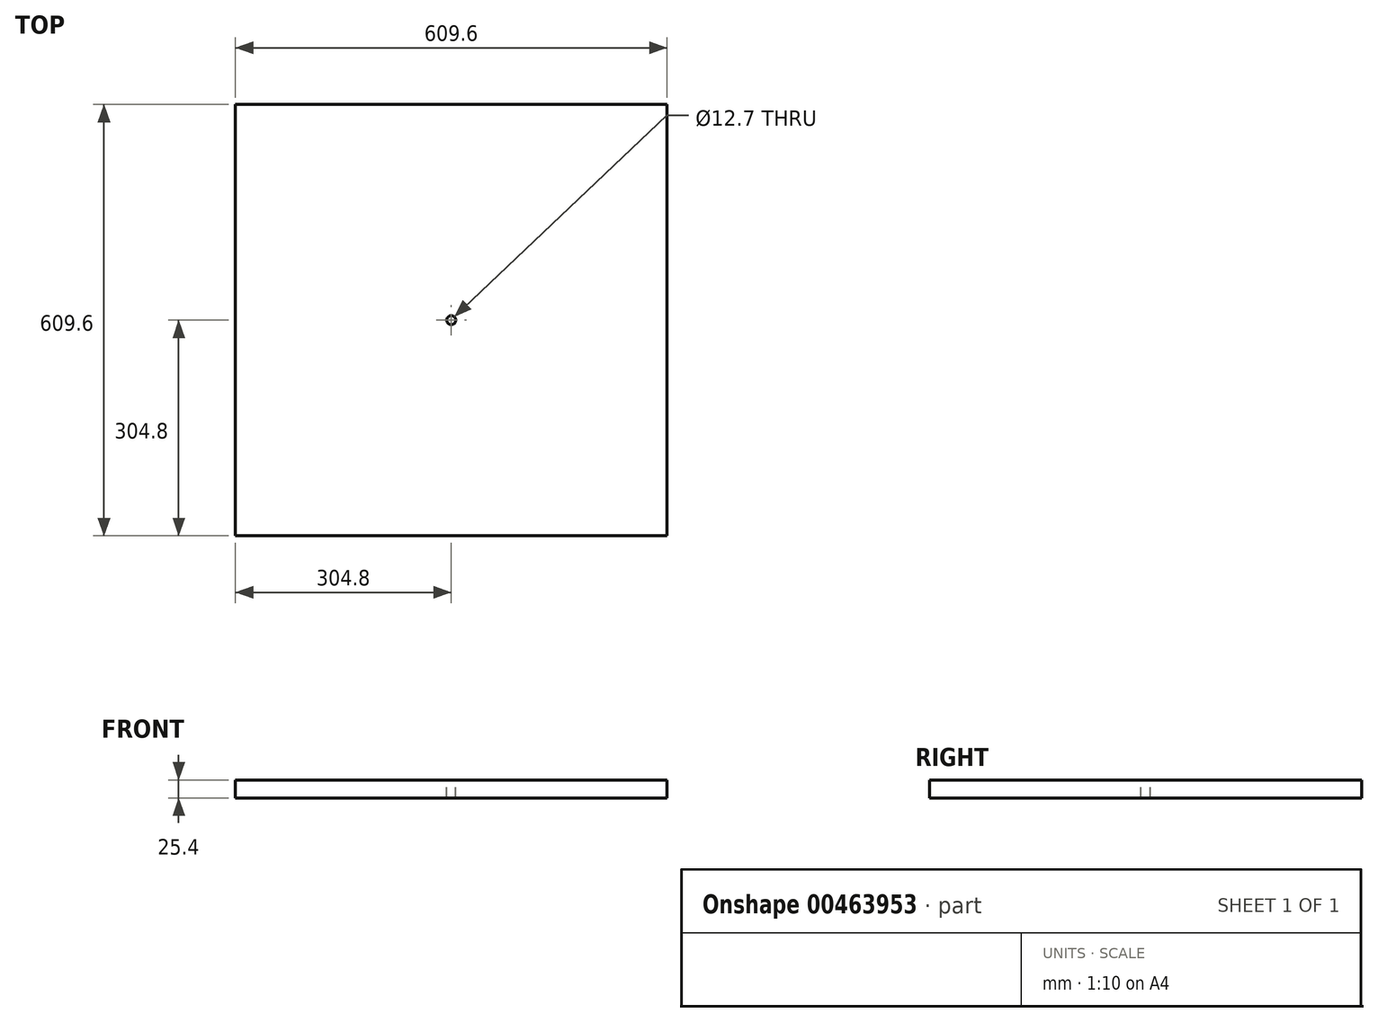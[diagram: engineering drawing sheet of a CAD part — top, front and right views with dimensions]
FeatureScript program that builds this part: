
annotation { "Feature Type Name" : "Feature", "Feature Type Description" : "" }
export const myFeature = defineFeature(function(context is Context, id is Id, definition is map)
    precondition{}
    {
        {
            var Q0;
            Q0=qCreatedBy(makeId("Top.planeOp"),FACE);
            var sketch = newSketch(context, id + "F0", { "sketchPlane" : qUnion([Q0])});
            skLineSegment(sketch, "E0.bottom", {"start": v(304.8, 304.8) * mm, "end": v(-304.8, 304.8) * mm});
            skLineSegment(sketch, "E0.top", {"start": v(304.8, -304.8) * mm, "end": v(-304.8, -304.8) * mm});
            skLineSegment(sketch, "E0.left", {"start": v(304.8, 304.8) * mm, "end": v(304.8, -304.8) * mm});
            skLineSegment(sketch, "E0.right", {"start": v(-304.8, 304.8) * mm, "end": v(-304.8, -304.8) * mm});
            skPoint(sketch, "E0.middle", {"position": v(0, 0) * mm});
            skSolve(sketch);
        }
        {
            var Q0;
            Q0 = qSketchRegion(id + "F0", true);
            extrude(context, id + "F1", {"entities" : qUnion([Q0]), "depth" : 25.4 * mm, "offsetDistance" : 25.4 * mm});
        }
        {
            var Q0;
            Q0=makeQuery(id+"F1.opExtrude","CAP_FACE",FACE,{"disambiguationData":[OSD([sQuery(id+"F0.wireOp",EDGE,"E0.bottom"),sQuery(id+"F0.wireOp",EDGE,"E0.top"),sQuery(id+"F0.wireOp",EDGE,"E0.left"),sQuery(id+"F0.wireOp",EDGE,"E0.right")])],"isStart":false});
            var sketch = newSketch(context, id + "F2", { "sketchPlane" : qUnion([Q0])});
            skCircle(sketch, "E1", {"center": v(0, 0) * mm, "radius": 6.35 * mm});
            skSolve(sketch);
        }
        {
            var Q0;
            Q0 = qSketchRegion(id + "F2", true);
            extrude(context, id + "F3", {"entities" : qUnion([Q0]), "operationType" : NewBodyOperationType.REMOVE, "endBound" : BoundingType.THROUGH_ALL, "oppositeDirection" : true, "depth" : 25.4 * mm, "offsetDistance" : 25.4 * mm});
        }
    });
